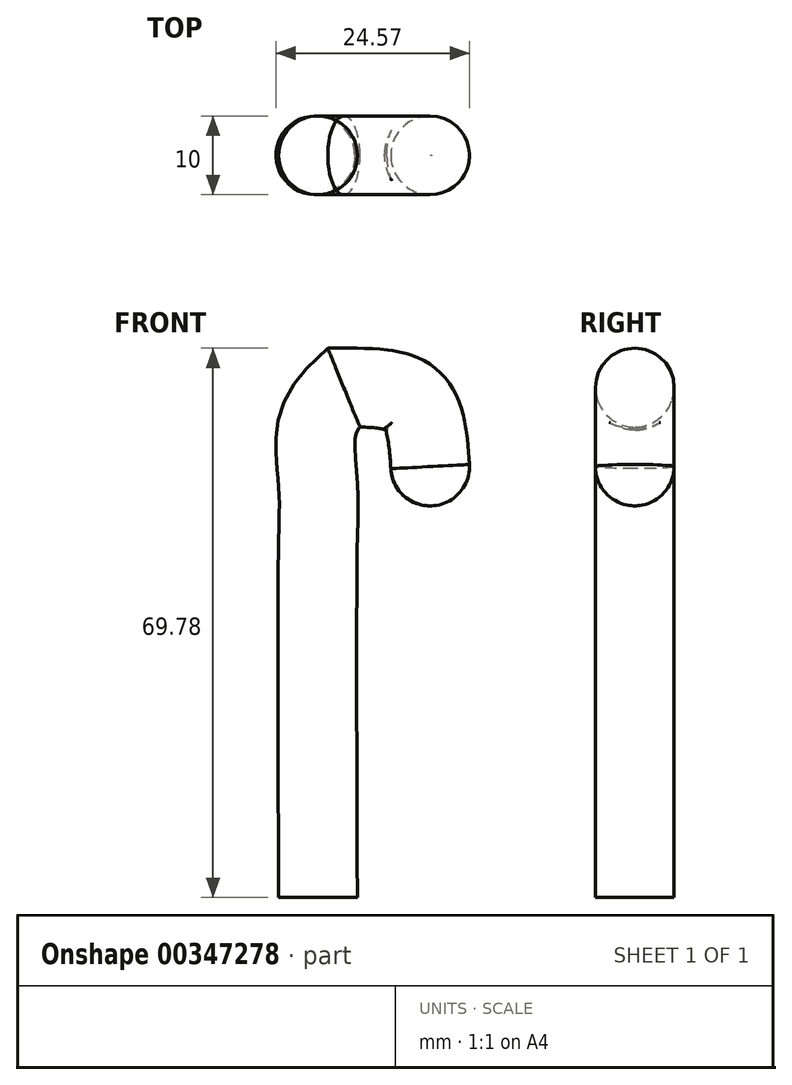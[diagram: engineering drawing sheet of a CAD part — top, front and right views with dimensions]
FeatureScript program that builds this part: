
annotation { "Feature Type Name" : "Feature", "Feature Type Description" : "" }
export const myFeature = defineFeature(function(context is Context, id is Id, definition is map)
    precondition{}
    {
        {
            var Q0;
            Q0=qCreatedBy(makeId("Front.planeOp"),FACE);
            var sketch = newSketch(context, id + "F0", { "sketchPlane" : qUnion([Q0])});
            skFitSpline(sketch, "E0", {"points": [v(0, 0) * mm, v(0, 45.54) * mm, v(0, 52.44) * mm, v(0, 60.24) * mm, v(3.27, 64.78) * mm], "startDerivative": vector(-0.53, 121.03) * mm, "endDerivative": vector(25.04, 24.03) * mm});
            skFitSpline(sketch, "E1", {"points": [v(3.27, 64.78) * mm, v(11.8, 63.33) * mm, v(13.97, 57.88) * mm, v(14.33, 52.26) * mm], "startDerivative": vector(26.5, 0.06) * mm, "endDerivative": vector(0.58, -17.77) * mm});
            skSolve(sketch);
        }
        {
            var Q0;
            Q0=qCreatedBy(makeId("Top.planeOp"),FACE);
            var sketch = newSketch(context, id + "F1", { "sketchPlane" : qUnion([Q0])});
            skCircle(sketch, "E2", {"center": v(0, 0) * mm, "radius": 5 * mm});
            skSolve(sketch);
        }
        {
            var Q0;
            Q0=makeQuery(id+"F1.imprint","IMPRINT",FACE,{"disambiguationData":[TD([[makeQuery(id+"F1.imprint","IMPRINT",EDGE,{"derivedFrom":sQuery(id+"F1.wireOp",EDGE,"E2")}),1.0]])]});
            var Q1;
            Q1=sQuery(id+"F0.wireOp",EDGE,"E1");
            var Q2;
            Q2=sQuery(id+"F0.wireOp",EDGE,"E0");
            sweep(context, id + "F2", {"profiles" : qUnion([Q0]), "path" : qUnion([Q1, Q2])});
        }
        {
            var Q0;
            Q0=makeQuery(id+"F2.opSweep","CAP_FACE",FACE,{"disambiguationData":[OSD([sQuery(id+"F0.wireOp",VERTEX,"E1.end"),sQuery(id+"F1.wireOp",EDGE,"E2")])],"isStart":false});
            extrude(context, id + "F3", {"entities" : qUnion([Q0]), "operationType" : NewBodyOperationType.ADD, "depth" : 2.5 * mm});
        }
        {
            var Q0;
            Q0=makeQuery(id+"F3.opExtrude","CAP_EDGE",EDGE,{"disambiguationData":[OSD([sQuery(id+"F0.wireOp",VERTEX,"E1.end"),sQuery(id+"F1.wireOp",EDGE,"E2")])],"isStart":false});
            fillet(context, id + "F4", {"entities" : qUnion([Q0]), "radius" : 5 * mm, "tangentPropagation" : true, "allowEdgeOverflow" : false});
        }
    });
